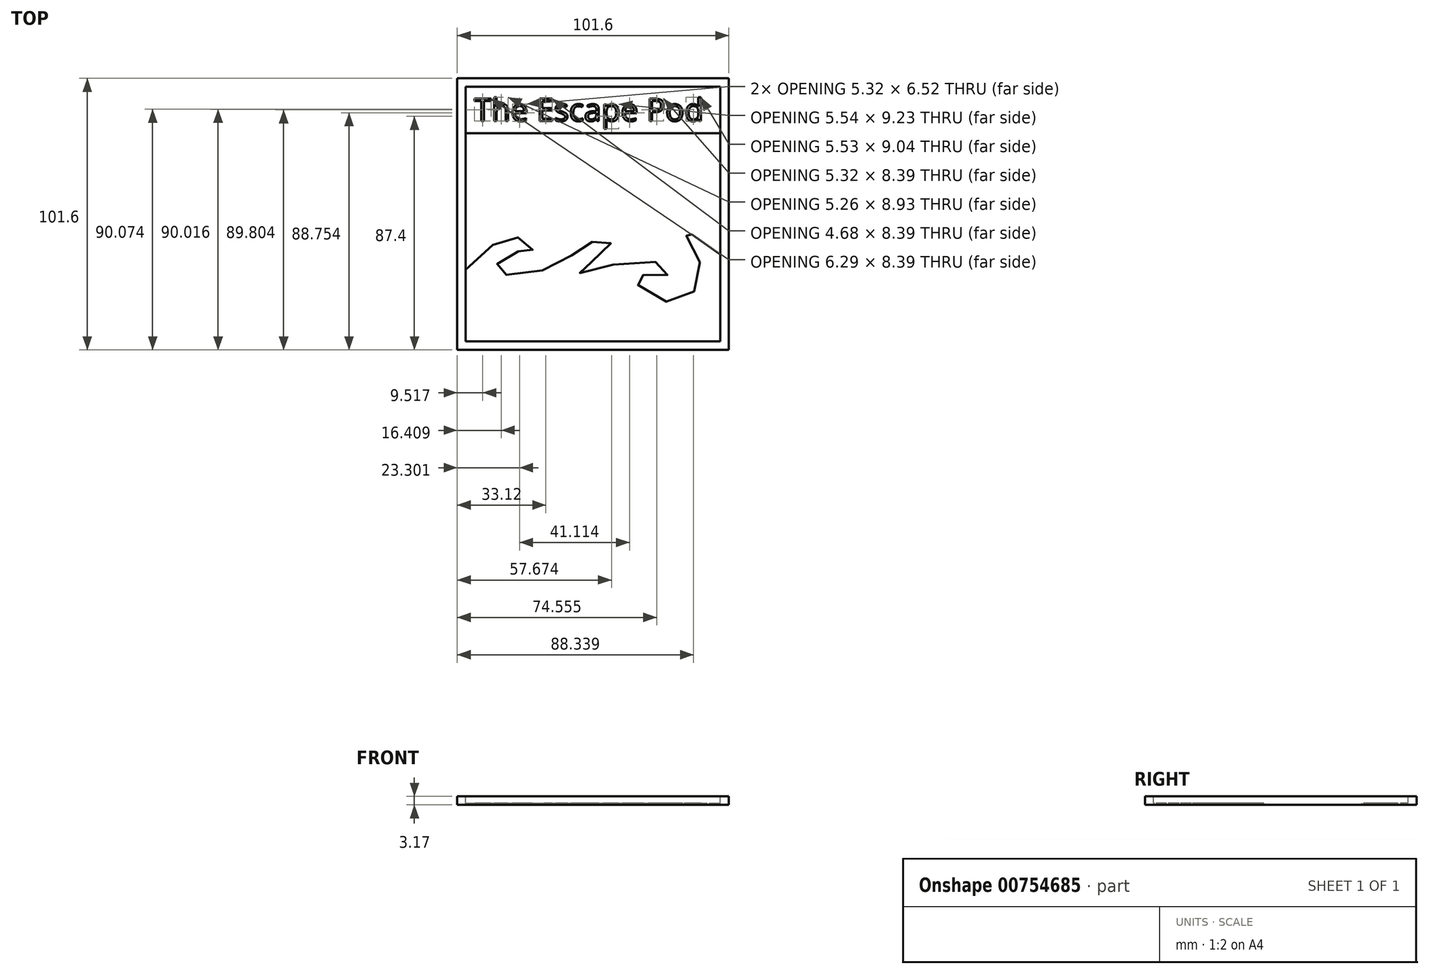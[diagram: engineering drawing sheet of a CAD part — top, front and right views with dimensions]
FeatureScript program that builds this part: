
annotation { "Feature Type Name" : "Feature", "Feature Type Description" : "" }
export const myFeature = defineFeature(function(context is Context, id is Id, definition is map)
    precondition{}
    {
        {
            var Q0;
            Q0=qCreatedBy(makeId("Top.planeOp"),FACE);
            var sketch = newSketch(context, id + "F0", { "sketchPlane" : qUnion([Q0])});
            skLineSegment(sketch, "E0.bottom", {"start": v(-54.3, 51.07) * mm, "end": v(47.3, 51.07) * mm});
            skLineSegment(sketch, "E0.top", {"start": v(-54.3, -50.53) * mm, "end": v(47.3, -50.53) * mm});
            skLineSegment(sketch, "E0.left", {"start": v(-54.3, 51.07) * mm, "end": v(-54.3, -50.53) * mm});
            skLineSegment(sketch, "E0.right", {"start": v(47.3, 51.07) * mm, "end": v(47.3, -50.53) * mm});
            skSolve(sketch);
        }
        {
            var Q0;
            Q0=makeQuery(id+"F0.imprint","IMPRINT",FACE,{"disambiguationData":[TD([[makeQuery(id+"F0.imprint","IMPRINT",EDGE,{"derivedFrom":sQuery(id+"F0.wireOp",EDGE,"E0.bottom")}),-1.0]])]});
            extrude(context, id + "F1", {"entities" : qUnion([Q0]), "depth" : 3.17 * mm, "offsetDistance" : 25.4 * mm});
        }
        {
            var Q0;
            Q0=makeQuery(id+"F1.opExtrude","CAP_FACE",FACE,{"disambiguationData":[OSD([sQuery(id+"F0.wireOp",EDGE,"E0.bottom"),sQuery(id+"F0.wireOp",EDGE,"E0.top"),sQuery(id+"F0.wireOp",EDGE,"E0.left"),sQuery(id+"F0.wireOp",EDGE,"E0.right")])],"isStart":false});
            var sketch = newSketch(context, id + "F2", { "sketchPlane" : qUnion([Q0])});
            skLineSegment(sketch, "E1.bottom", {"start": v(-51.13, 47.9) * mm, "end": v(44.12, 47.9) * mm});
            skLineSegment(sketch, "E1.top", {"start": v(-51.13, -47.36) * mm, "end": v(44.12, -47.36) * mm});
            skLineSegment(sketch, "E1.left", {"start": v(-51.13, 47.9) * mm, "end": v(-51.13, -47.36) * mm});
            skLineSegment(sketch, "E1.right", {"start": v(44.12, 47.9) * mm, "end": v(44.12, -47.36) * mm});
            skSolve(sketch);
        }
        {
            var Q0;
            Q0 = qSketchRegion(id + "F2", true);
            extrude(context, id + "F3", {"entities" : qUnion([Q0]), "operationType" : NewBodyOperationType.REMOVE, "oppositeDirection" : true, "depth" : 2.54 * mm, "offsetDistance" : 25.4 * mm});
        }
        {
            var Q0;
            Q0=makeQuery(id+"F3.boolean.opBoolean","COPY",FACE,{"derivedFrom":makeQuery(id+"F3.opExtrude","CAP_FACE",FACE,{"disambiguationData":[OSD([sQuery(id+"F2.wireOp",EDGE,"E1.bottom"),sQuery(id+"F2.wireOp",EDGE,"E1.top"),sQuery(id+"F2.wireOp",EDGE,"E1.left"),sQuery(id+"F2.wireOp",EDGE,"E1.right")])],"isStart":false})});
            var sketch = newSketch(context, id + "F4", { "sketchPlane" : qUnion([Q0])});
            skFitSpline(sketch, "E2", {"points": [v(-51.13, -20.53) * mm, v(-32.18, -8.26) * mm, v(-26.17, -13.27) * mm, v(-32.43, -13.77) * mm, v(-39.94, -20.79) * mm, v(-18.16, -19.28) * mm, v(-3.63, -10.02) * mm, v(3.13, -11.02) * mm, v(-9.14, -21.54) * mm, v(18.4, -17.28) * mm, v(24.17, -22.54) * mm, v(12.15, -23.04) * mm, v(24.67, -32.55) * mm, v(36.94, -20.53) * mm, v(30.68, -6.26) * mm, v(44.12, -14.77) * mm], "startDerivative": vector(236.54, 238.34) * mm, "endDerivative": vector(280.15, -203.35) * mm});
            skLineSegment(sketch, "E3", {"start": v(-51.13, 30.55) * mm, "end": v(44.12, 30.55) * mm});
            skSolve(sketch);
        }
        {
            var Q0;
            {var subQ0=sQuery(id+"F4.wireOp",EDGE,"E2");Q0=makeQuery(id+"F4.imprint","IMPRINT",FACE,{"disambiguationData":[TD([[makeQuery(id+"F4.imprint","IMPRINT",EDGE,{"derivedFrom":subQ0}),1.0]])]});}
            extrude(context, id + "F5", {"entities" : qUnion([Q0]), "operationType" : NewBodyOperationType.REMOVE, "oppositeDirection" : true, "depth" : 25.4 * mm, "offsetDistance" : 25.4 * mm});
        }
        {
            var Q0;
            {var subQ0=sQuery(id+"F2.wireOp",EDGE,"E1.right");var subQ1=sQuery(id+"F2.wireOp",EDGE,"E1.left");var subQ2=sQuery(id+"F2.wireOp",EDGE,"E1.bottom");Q0=makeQuery(id+"F5.boolean.opBoolean","SPLIT",FACE,{"disambiguationData":[TD([makeQuery(id+"F3.boolean.opBoolean","COPY",FACE,{"derivedFrom":makeQuery(id+"F3.opExtrude","SWEPT_FACE",FACE,{"disambiguationData":[OSD([subQ2])]})})])],"derivedFrom":makeQuery(id+"F3.boolean.opBoolean","COPY",FACE,{"derivedFrom":makeQuery(id+"F3.opExtrude","CAP_FACE",FACE,{"disambiguationData":[OSD([subQ2,sQuery(id+"F2.wireOp",EDGE,"E1.top"),subQ1,subQ0])],"isStart":false})})});}
            var sketch = newSketch(context, id + "F6", { "sketchPlane" : qUnion([Q0])});
            skText(sketch, "E4", { "text": "The Escape Pod", "fontName": "OpenSans-Regular.ttf"});
            const initialGuessF6  = {"E4": [-0.04804, 0.03508, 1, 0, 0.00846]};
            skSetInitialGuess(sketch, initialGuessF6);
            skSolve(sketch);
        }
        {
            var Q0;
            Q0 = qSketchRegion(id + "F6", true);
            extrude(context, id + "F7", {"entities" : qUnion([Q0]), "operationType" : NewBodyOperationType.REMOVE, "oppositeDirection" : true, "depth" : 2.54 * mm, "offsetDistance" : 25.4 * mm});
        }
        {
            var Q0;
            {var subQ0=sQuery(id+"F2.wireOp",EDGE,"E1.right");var subQ1=sQuery(id+"F2.wireOp",EDGE,"E1.left");var subQ2=sQuery(id+"F2.wireOp",EDGE,"E1.top");Q0=makeQuery(id+"F5.boolean.opBoolean","SPLIT",FACE,{"disambiguationData":[TD([makeQuery(id+"F3.boolean.opBoolean","COPY",FACE,{"derivedFrom":makeQuery(id+"F3.opExtrude","SWEPT_FACE",FACE,{"disambiguationData":[OSD([subQ2])]})})])],"derivedFrom":makeQuery(id+"F3.boolean.opBoolean","COPY",FACE,{"derivedFrom":makeQuery(id+"F3.opExtrude","CAP_FACE",FACE,{"disambiguationData":[OSD([sQuery(id+"F2.wireOp",EDGE,"E1.bottom"),subQ2,subQ1,subQ0])],"isStart":false})})});}
            var sketch = newSketch(context, id + "F8", { "sketchPlane" : qUnion([Q0])});
            skLineSegment(sketch, "E5", {"start": v(-41.6, -34.77) * mm, "end": v(0, -34.77) * mm});
            skSolve(sketch);
        }
        {
            var Q0;
            Q0=sQuery(id+"F8.wireOp",EDGE,"E5");
            extrude(context, id + "F9", {"bodyType" : ToolBodyType.SURFACE, "surfaceEntities" : qUnion([Q0]), "depth" : 2.54 * mm, "offsetDistance" : 25.4 * mm});
        }
    });
